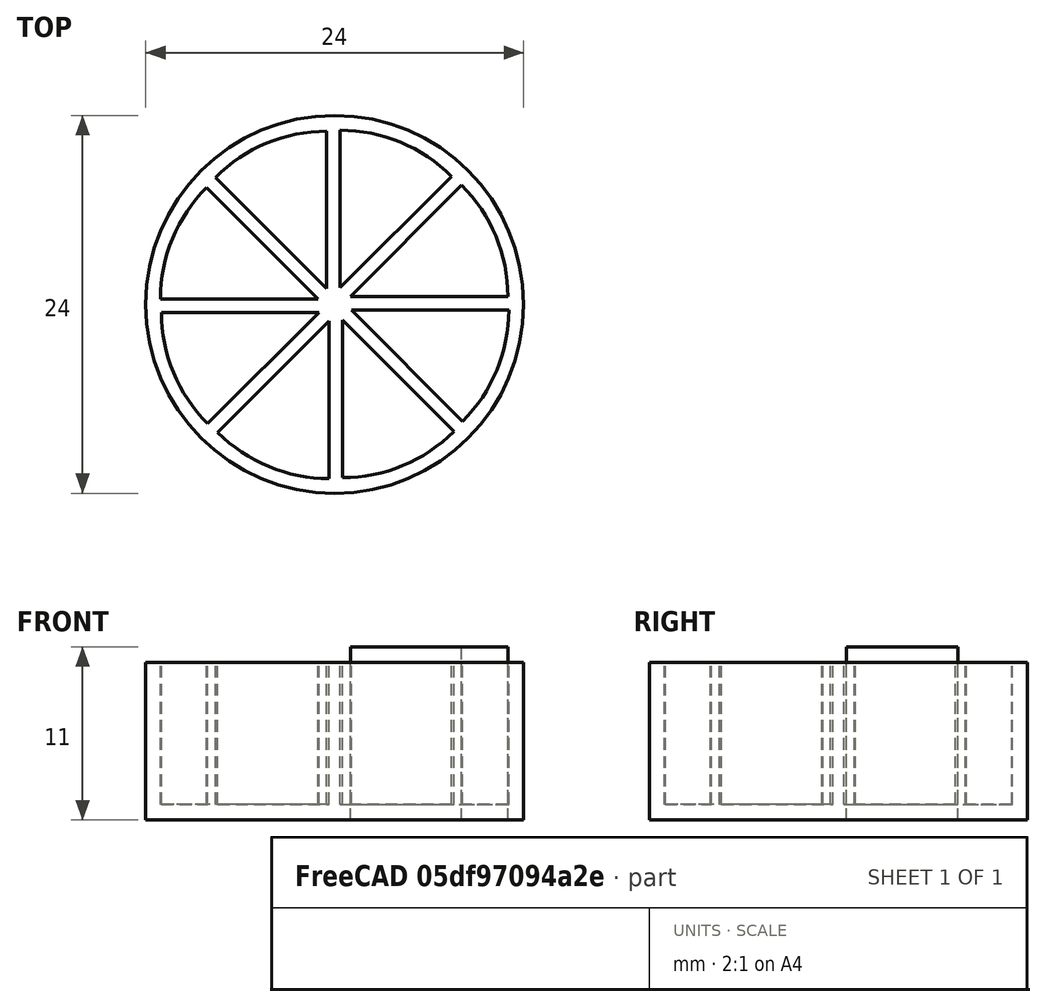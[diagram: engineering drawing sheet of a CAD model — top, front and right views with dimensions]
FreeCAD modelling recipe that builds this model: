
FCSTD DOCUMENT  (FreeCAD 0.21R33694 (Git))
Label: OJT1_T11P02.45gr
License: All rights reserved
LicenseURL: http://en.wikipedia.org/wiki/All_rights_reserved
objects: Part::Cylinder×3, Part::FeaturePython×1, Part::Cut×1
note: 4 computed .brp shape members not serialized (recipe doc carries the construction recipe); baked Part::Feature solids carry a one-line shape summary decoded from their .brp

FEATURE [Part::Cylinder] Cylinder  label="Cilindre"
  Angle = 360
  AttacherType = Attacher::AttachEngine3D
  FirstAngle = 0
  Height = 10
  Radius = 12
  SecondAngle = 0
FEATURE [Part::Cylinder] Cylinder001  label="Cilindre001"
  Angle = 45
  AttacherType = Attacher::AttachEngine3D
  FirstAngle = 0
  Height = 10
  Placement = pos=(1,0.5,0) rot=(0,0,1;0rad)
  Radius = 10
  SecondAngle = 0
FEATURE [Part::FeaturePython] Array  # Draft array (typed FeaturePython)
  AlwaysSyncPlacement = false
  Angle = 360
  ArrayType = 1
  Axis = (0,0,1)
  Base = -> Cylinder001
  Center = (0,0,0)
  Count = 8
  ExpandArray = false
  Fuse = false
  IntervalAxis = (0,0,0)
  IntervalX = (50,0,0)
  IntervalY = (0,50,0)
  IntervalZ = (0,0,50)
  NumberCircles = 3
  NumberPolar = 8
  NumberX = 2
  NumberY = 2
  NumberZ = 1
  Placement = pos=(0,0,1) rot=(0,0,1;0rad)
  PlacementList = 8 placements: [(1,0.5,0),(0.353553,1.06066,0),(-0.5,1,0),(-1.06066,0.353553,0),(-1,-0.5,0),(-0.353553,-1.06066,0),(0.5,-1,0),(1.06066,-0.353553,0)]
  RadialDistance = 50
  ScaleList = (8) [(1,1,1),(1,1,1),(1,1,1),(1,1,1),(1,1,1),(1,1,1),(1,1,1),(1,1,1)]
  Symmetry = 1
  TangentialDistance = 25
FEATURE [Part::Cylinder] Cylinder002  label="Cilindre002"
  Angle = 45
  AttacherType = Attacher::AttachEngine3D
  FirstAngle = 0
  Height = 10
  Placement = pos=(1,0.5,1) rot=(0,0,1;0rad)
  Radius = 10
  SecondAngle = 0
FEATURE [Part::Cut] Cut
  Base = -> Cylinder
  Refine = true
  Tool = -> Array
